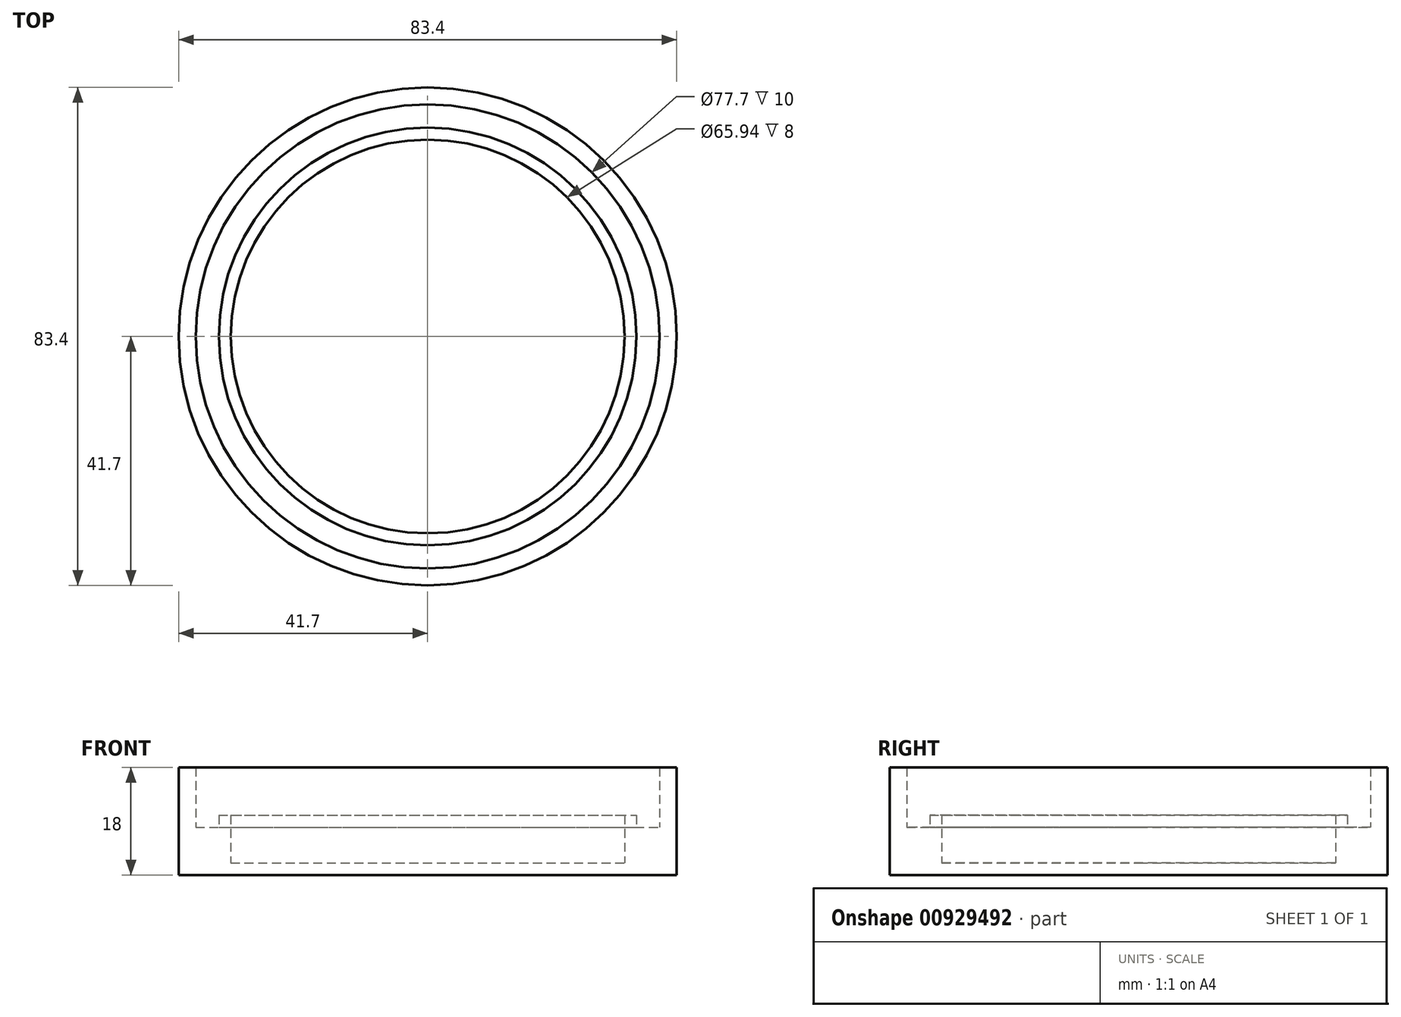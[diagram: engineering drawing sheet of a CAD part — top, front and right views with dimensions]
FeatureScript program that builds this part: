
annotation { "Feature Type Name" : "Feature", "Feature Type Description" : "" }
export const myFeature = defineFeature(function(context is Context, id is Id, definition is map)
    precondition{}
    {
        {
            var Q0;
            Q0=qCreatedBy(makeId("Front.planeOp"),FACE);
            var sketch = newSketch(context, id + "F0", { "sketchPlane" : qUnion([Q0])});
            skLineSegment(sketch, "E0", {"start": v(0, 0) * mm, "end": v(32.97, 0) * mm});
            skLineSegment(sketch, "E1", {"start": v(32.97, 0) * mm, "end": v(32.97, 8) * mm});
            skLineSegment(sketch, "E2", {"start": v(32.97, 8) * mm, "end": v(34.97, 8) * mm});
            skLineSegment(sketch, "E3", {"start": v(34.97, 8) * mm, "end": v(34.97, 6) * mm});
            skLineSegment(sketch, "E4", {"start": v(34.97, 6) * mm, "end": v(38.85, 6) * mm});
            skLineSegment(sketch, "E5", {"start": v(38.85, 6) * mm, "end": v(38.85, 16) * mm});
            skLineSegment(sketch, "E6", {"start": v(38.85, 16) * mm, "end": v(41.7, 16) * mm});
            skLineSegment(sketch, "E7", {"start": v(41.7, 16) * mm, "end": v(41.7, -2) * mm});
            skLineSegment(sketch, "E8", {"start": v(41.7, -2) * mm, "end": v(0, -2) * mm});
            skLineSegment(sketch, "E9", {"start": v(0, -2) * mm, "end": v(0, 0) * mm});
            skPoint(sketch, "E10", {"position": v(0, 16) * mm});
            skSolve(sketch);
        }
        {
            var Q0;
            Q0=makeQuery(id+"F0.imprint","IMPRINT",FACE,{"disambiguationData":[TD([[makeQuery(id+"F0.imprint","IMPRINT",EDGE,{"derivedFrom":sQuery(id+"F0.wireOp",EDGE,"E0")}),-1.0]])]});
            var Q1;
            Q1=sQuery(id+"F0.wireOp",EDGE,"E9");
            revolve(context, id + "F1", {"surfaceOperationType" : NewSurfaceOperationType.NEW, "entities" : qUnion([Q0]), "axis" : qUnion([Q1]), "revolveType" : RevolveType.FULL});
        }
    });
